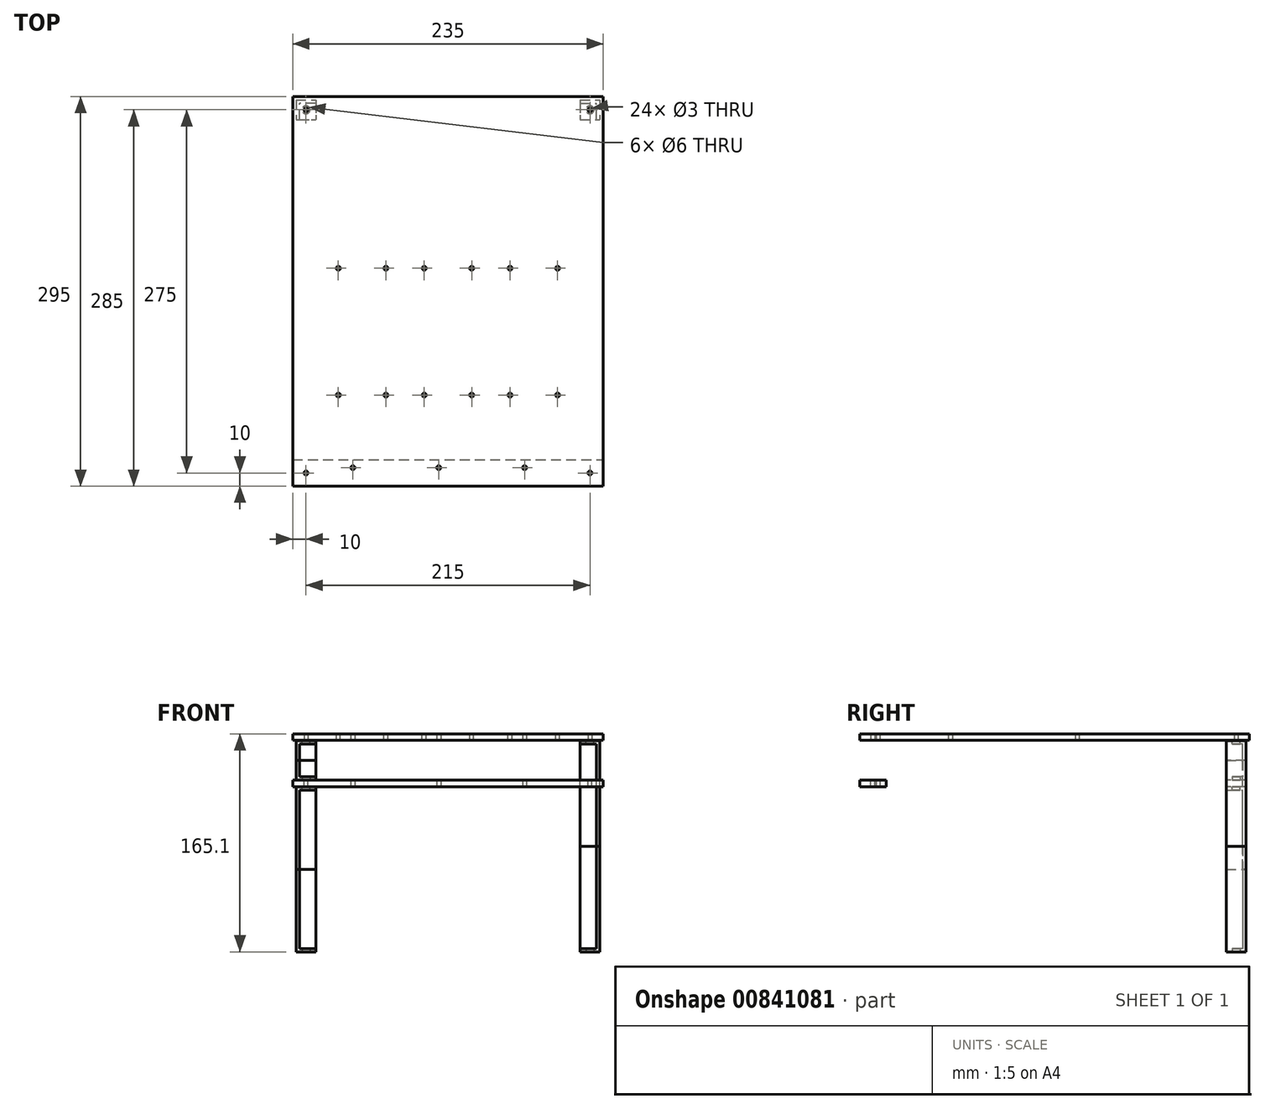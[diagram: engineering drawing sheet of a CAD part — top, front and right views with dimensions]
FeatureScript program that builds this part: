
annotation { "Feature Type Name" : "Feature", "Feature Type Description" : "" }
export const myFeature = defineFeature(function(context is Context, id is Id, definition is map)
    precondition{}
    {
        {
            var Q0;
            Q0=qCreatedBy(makeId("Top.planeOp"),FACE);
            var sketch = newSketch(context, id + "F0", { "sketchPlane" : qUnion([Q0])});
            skLineSegment(sketch, "E0.bottom", {"start": v(-22.5, 0) * mm, "end": v(22.5, 0) * mm});
            skLineSegment(sketch, "E0.top", {"start": v(-22.5, 130) * mm, "end": v(22.5, 130) * mm});
            skLineSegment(sketch, "E0.left", {"start": v(-22.5, 0) * mm, "end": v(-22.5, 130) * mm});
            skLineSegment(sketch, "E0.right", {"start": v(22.5, 0) * mm, "end": v(22.5, 130) * mm});
            skLineSegment(sketch, "E1.bottom", {"start": v(42.5, 0) * mm, "end": v(87.5, 0) * mm});
            skLineSegment(sketch, "E1.top", {"start": v(42.5, 130) * mm, "end": v(87.5, 130) * mm});
            skLineSegment(sketch, "E1.left", {"start": v(42.5, 0) * mm, "end": v(42.5, 130) * mm});
            skLineSegment(sketch, "E1.right", {"start": v(87.5, 0) * mm, "end": v(87.5, 130) * mm});
            skLineSegment(sketch, "E2.bottom", {"start": v(-42.5, 0) * mm, "end": v(-87.5, 0) * mm});
            skLineSegment(sketch, "E2.top", {"start": v(-42.5, 130) * mm, "end": v(-87.5, 130) * mm});
            skLineSegment(sketch, "E2.left", {"start": v(-42.5, 0) * mm, "end": v(-42.5, 130) * mm});
            skLineSegment(sketch, "E2.right", {"start": v(-87.5, 0) * mm, "end": v(-87.5, 130) * mm});
            skCircle(sketch, "E3", {"center": v(-83, 4) * mm, "radius": 1.5 * mm});
            skCircle(sketch, "E4", {"center": v(-47, 4) * mm, "radius": 1.5 * mm});
            skCircle(sketch, "E5", {"center": v(-47, 100) * mm, "radius": 1.5 * mm});
            skCircle(sketch, "E6", {"center": v(-83, 100) * mm, "radius": 1.5 * mm});
            skLineSegment(sketch, "E7", {"start": v(-47, 100) * mm, "end": v(-47, 4) * mm, "construction": true});
            skLineSegment(sketch, "E8", {"start": v(-47, 52) * mm, "end": v(0, 52) * mm, "construction": true});
            skLineSegment(sketch, "E9", {"start": v(0, 52) * mm, "end": v(65, 52) * mm, "construction": true});
            skPoint(sketch, "E9.endSnap0", {"position": v(65, 0) * mm});
            skLineSegment(sketch, "E10.bottom", {"start": v(-18, 4) * mm, "end": v(18, 4) * mm, "construction": true});
            skLineSegment(sketch, "E10.top", {"start": v(-18, 100) * mm, "end": v(18, 100) * mm, "construction": true});
            skLineSegment(sketch, "E10.left", {"start": v(-18, 4) * mm, "end": v(-18, 100) * mm, "construction": true});
            skLineSegment(sketch, "E10.right", {"start": v(18, 4) * mm, "end": v(18, 100) * mm, "construction": true});
            skPoint(sketch, "E10.middle", {"position": v(0, 52) * mm});
            skLineSegment(sketch, "E11.bottom", {"start": v(83, 4) * mm, "end": v(47, 4) * mm, "construction": true});
            skLineSegment(sketch, "E11.top", {"start": v(83, 100) * mm, "end": v(47, 100) * mm, "construction": true});
            skLineSegment(sketch, "E11.left", {"start": v(83, 4) * mm, "end": v(83, 100) * mm, "construction": true});
            skLineSegment(sketch, "E11.right", {"start": v(47, 4) * mm, "end": v(47, 100) * mm, "construction": true});
            skPoint(sketch, "E11.middle", {"position": v(65, 52) * mm});
            skCircle(sketch, "E12", {"center": v(-18, 100) * mm, "radius": 1.5 * mm});
            skCircle(sketch, "E13", {"center": v(18, 100) * mm, "radius": 1.5 * mm});
            skCircle(sketch, "E14", {"center": v(18, 4) * mm, "radius": 1.5 * mm});
            skCircle(sketch, "E15", {"center": v(-18, 4) * mm, "radius": 1.5 * mm});
            skCircle(sketch, "E16", {"center": v(47, 4) * mm, "radius": 1.5 * mm});
            skCircle(sketch, "E17", {"center": v(83, 4) * mm, "radius": 1.5 * mm});
            skCircle(sketch, "E18", {"center": v(47, 100) * mm, "radius": 1.5 * mm});
            skCircle(sketch, "E19", {"center": v(83, 100) * mm, "radius": 1.5 * mm});
            skLineSegment(sketch, "E20", {"start": v(-72, 42.63) * mm, "end": v(-72, -107.37) * mm, "construction": true});
            skLineSegment(sketch, "E21", {"start": v(-7, 42.63) * mm, "end": v(-7, -107.37) * mm, "construction": true});
            skLineSegment(sketch, "E22", {"start": v(58, 42.63) * mm, "end": v(58, -107.37) * mm, "construction": true});
            skSolve(sketch);
        }
        {
            var Q0;
            Q0=qCreatedBy(makeId("Top.planeOp"),FACE);
            var sketch = newSketch(context, id + "F1", { "sketchPlane" : qUnion([Q0])});
            skLineSegment(sketch, "E23.bottom", {"start": v(-117.5, 230) * mm, "end": v(117.5, 230) * mm});
            skLineSegment(sketch, "E23.top", {"start": v(-117.5, -65) * mm, "end": v(117.5, -65) * mm});
            skLineSegment(sketch, "E23.left", {"start": v(-117.5, 230) * mm, "end": v(-117.5, -65) * mm});
            skLineSegment(sketch, "E23.right", {"start": v(117.5, 230) * mm, "end": v(117.5, -65) * mm});
            skLineSegment(sketch, "E24", {"start": v(-117.5, -45) * mm, "end": v(117.5, -45) * mm, "construction": true});
            skSolve(sketch);
        }
        {
            var Q0;
            Q0=makeQuery(id+"F1.imprint","IMPRINT",FACE,{"disambiguationData":[TD([[makeQuery(id+"F1.imprint","IMPRINT",EDGE,{"derivedFrom":sQuery(id+"F1.wireOp",EDGE,"E23.bottom")}),-1.0]])]});
            extrude(context, id + "F2", {"entities" : qUnion([Q0]), "oppositeDirection" : true, "depth" : 5 * mm, "offsetDistance" : 25 * mm});
        }
        {
            var Q0;
            Q0=makeQuery(id+"F0.imprint","IMPRINT",FACE,{"disambiguationData":[TD([[makeQuery(id+"F0.imprint","IMPRINT",EDGE,{"derivedFrom":sQuery(id+"F0.wireOp",EDGE,"E5")}),1.0]])]});
            var Q1;
            Q1=makeQuery(id+"F0.imprint","IMPRINT",FACE,{"disambiguationData":[TD([[makeQuery(id+"F0.imprint","IMPRINT",EDGE,{"derivedFrom":sQuery(id+"F0.wireOp",EDGE,"E6")}),1.0]])]});
            var Q2;
            Q2=makeQuery(id+"F0.imprint","IMPRINT",FACE,{"disambiguationData":[TD([[makeQuery(id+"F0.imprint","IMPRINT",EDGE,{"derivedFrom":sQuery(id+"F0.wireOp",EDGE,"E3")}),1.0]])]});
            var Q3;
            Q3=makeQuery(id+"F0.imprint","IMPRINT",FACE,{"disambiguationData":[TD([[makeQuery(id+"F0.imprint","IMPRINT",EDGE,{"derivedFrom":sQuery(id+"F0.wireOp",EDGE,"E4")}),1.0]])]});
            var Q4;
            Q4=makeQuery(id+"F0.imprint","IMPRINT",FACE,{"disambiguationData":[TD([[makeQuery(id+"F0.imprint","IMPRINT",EDGE,{"derivedFrom":sQuery(id+"F0.wireOp",EDGE,"E15")}),1.0]])]});
            var Q5;
            Q5=makeQuery(id+"F0.imprint","IMPRINT",FACE,{"disambiguationData":[TD([[makeQuery(id+"F0.imprint","IMPRINT",EDGE,{"derivedFrom":sQuery(id+"F0.wireOp",EDGE,"E14")}),1.0]])]});
            var Q6;
            Q6=makeQuery(id+"F0.imprint","IMPRINT",FACE,{"disambiguationData":[TD([[makeQuery(id+"F0.imprint","IMPRINT",EDGE,{"derivedFrom":sQuery(id+"F0.wireOp",EDGE,"E12")}),1.0]])]});
            var Q7;
            Q7=makeQuery(id+"F0.imprint","IMPRINT",FACE,{"disambiguationData":[TD([[makeQuery(id+"F0.imprint","IMPRINT",EDGE,{"derivedFrom":sQuery(id+"F0.wireOp",EDGE,"E13")}),1.0]])]});
            var Q8;
            Q8=makeQuery(id+"F0.imprint","IMPRINT",FACE,{"disambiguationData":[TD([[makeQuery(id+"F0.imprint","IMPRINT",EDGE,{"derivedFrom":sQuery(id+"F0.wireOp",EDGE,"E18")}),1.0]])]});
            var Q9;
            Q9=makeQuery(id+"F0.imprint","IMPRINT",FACE,{"disambiguationData":[TD([[makeQuery(id+"F0.imprint","IMPRINT",EDGE,{"derivedFrom":sQuery(id+"F0.wireOp",EDGE,"E19")}),1.0]])]});
            var Q10;
            Q10=makeQuery(id+"F0.imprint","IMPRINT",FACE,{"disambiguationData":[TD([[makeQuery(id+"F0.imprint","IMPRINT",EDGE,{"derivedFrom":sQuery(id+"F0.wireOp",EDGE,"E17")}),1.0]])]});
            var Q11;
            Q11=makeQuery(id+"F0.imprint","IMPRINT",FACE,{"disambiguationData":[TD([[makeQuery(id+"F0.imprint","IMPRINT",EDGE,{"derivedFrom":sQuery(id+"F0.wireOp",EDGE,"E16")}),1.0]])]});
            extrude(context, id + "F3", {"entities" : qUnion([Q0, Q1, Q2, Q3, Q4, Q5, Q6, Q7, Q8, Q9, Q10, Q11]), "operationType" : NewBodyOperationType.REMOVE, "endBound" : BoundingType.THROUGH_ALL, "oppositeDirection" : true, "depth" : 25 * mm, "offsetDistance" : 25 * mm});
        }
        {
            var Q0;
            Q0=makeQuery(id+"F2.opExtrude","CAP_FACE",FACE,{"disambiguationData":[OSD([sQuery(id+"F1.wireOp",EDGE,"E23.bottom"),sQuery(id+"F1.wireOp",EDGE,"E23.top"),sQuery(id+"F1.wireOp",EDGE,"E23.left"),sQuery(id+"F1.wireOp",EDGE,"E23.right")])],"isStart":false});
            var sketch = newSketch(context, id + "F4", { "sketchPlane" : qUnion([Q0])});
            skLineSegment(sketch, "E25", {"start": v(117.5, -230) * mm, "end": v(-117.5, 65) * mm, "construction": true});
            skLineSegment(sketch, "E26.bottom", {"start": v(107.5, 55) * mm, "end": v(-107.5, 55) * mm, "construction": true});
            skLineSegment(sketch, "E26.top", {"start": v(107.5, -220) * mm, "end": v(-107.5, -220) * mm, "construction": true});
            skLineSegment(sketch, "E26.left", {"start": v(107.5, 55) * mm, "end": v(107.5, -220) * mm, "construction": true});
            skLineSegment(sketch, "E26.right", {"start": v(-107.5, 55) * mm, "end": v(-107.5, -220) * mm, "construction": true});
            skPoint(sketch, "E26.middle", {"position": v(0, -82.5) * mm});
            skCircle(sketch, "E27", {"center": v(107.5, -220) * mm, "radius": 1.5 * mm});
            skCircle(sketch, "E28", {"center": v(-107.5, -220) * mm, "radius": 1.5 * mm});
            skCircle(sketch, "E29", {"center": v(-107.5, 55) * mm, "radius": 1.5 * mm});
            skCircle(sketch, "E30", {"center": v(107.5, 55) * mm, "radius": 1.5 * mm});
            skSolve(sketch);
        }
        {
            var Q0;
            Q0=makeQuery(id+"F4.imprint","IMPRINT",FACE,{"disambiguationData":[TD([[makeQuery(id+"F4.imprint","IMPRINT",EDGE,{"derivedFrom":sQuery(id+"F4.wireOp",EDGE,"E27")}),1.0]])]});
            var Q1;
            Q1=makeQuery(id+"F4.imprint","IMPRINT",FACE,{"disambiguationData":[TD([[makeQuery(id+"F4.imprint","IMPRINT",EDGE,{"derivedFrom":sQuery(id+"F4.wireOp",EDGE,"E30")}),1.0]])]});
            var Q2;
            Q2=makeQuery(id+"F4.imprint","IMPRINT",FACE,{"disambiguationData":[TD([[makeQuery(id+"F4.imprint","IMPRINT",EDGE,{"derivedFrom":sQuery(id+"F4.wireOp",EDGE,"E29")}),1.0]])]});
            var Q3;
            Q3=makeQuery(id+"F4.imprint","IMPRINT",FACE,{"disambiguationData":[TD([[makeQuery(id+"F4.imprint","IMPRINT",EDGE,{"derivedFrom":sQuery(id+"F4.wireOp",EDGE,"E28")}),1.0]])]});
            var Q4;
            Q4=sQuery(id+"F4.wireOp",EDGE,"E27");
            extrude(context, id + "F5", {"entities" : qUnion([Q0, Q1, Q2, Q3]), "operationType" : NewBodyOperationType.REMOVE, "surfaceEntities" : qUnion([Q4]), "endBound" : BoundingType.THROUGH_ALL, "oppositeDirection" : true, "depth" : 25 * mm, "offsetDistance" : 25 * mm});
        }
        {
            var Q0;
            Q0=makeQuery(id+"F2.opExtrude","CAP_FACE",FACE,{"disambiguationData":[OSD([sQuery(id+"F1.wireOp",EDGE,"E23.bottom"),sQuery(id+"F1.wireOp",EDGE,"E23.top"),sQuery(id+"F1.wireOp",EDGE,"E23.left"),sQuery(id+"F1.wireOp",EDGE,"E23.right")])],"isStart":false});
            cPlane(context, id + "F6", {"entities" : qUnion([Q0]), "cplaneType" : CPlaneType.OFFSET, "offset" : 0.1 * mm, "width" : 150 * mm, "height" : 150 * mm});
        }
        {
            var Q0;
            Q0=qCreatedBy(id+"F6.planeOp",FACE);
            var sketch = newSketch(context, id + "F7", { "sketchPlane" : qUnion([Q0])});
            skCircle(sketch, "E31.0", {"center": v(-107.5, -220) * mm, "radius": 1.5 * mm, "construction": true});
            skCircle(sketch, "E32", {"center": v(-107.5, -220) * mm, "radius": 3 * mm});
            skLineSegment(sketch, "E33.bottom", {"start": v(-115, -227.5) * mm, "end": v(-100, -227.5) * mm});
            skLineSegment(sketch, "E33.top", {"start": v(-115, -212.5) * mm, "end": v(-100, -212.5) * mm});
            skLineSegment(sketch, "E33.left", {"start": v(-115, -227.5) * mm, "end": v(-115, -212.5) * mm});
            skLineSegment(sketch, "E33.right", {"start": v(-100, -227.5) * mm, "end": v(-100, -212.5) * mm});
            skSolve(sketch);
        }
        {
            var Q0;
            Q0=makeQuery(id+"F7.imprint","IMPRINT",FACE,{"disambiguationData":[TD([[makeQuery(id+"F7.imprint","IMPRINT",EDGE,{"derivedFrom":sQuery(id+"F7.wireOp",EDGE,"E32")}),-1.0]])]});
            extrude(context, id + "F8", {"entities" : qUnion([Q0]), "depth" : 2.5 * mm, "offsetDistance" : 25 * mm});
        }
        {
            var Q0;
            Q0=makeQuery(id+"F8.opExtrude","CAP_FACE",FACE,{"disambiguationData":[OSD([sQuery(id+"F7.wireOp",EDGE,"E32"),sQuery(id+"F7.wireOp",EDGE,"E33.bottom"),sQuery(id+"F7.wireOp",EDGE,"E33.top"),sQuery(id+"F7.wireOp",EDGE,"E33.left"),sQuery(id+"F7.wireOp",EDGE,"E33.right")])],"isStart":false});
            var sketch = newSketch(context, id + "F9", { "sketchPlane" : qUnion([Q0])});
            skLineSegment(sketch, "E34", {"start": v(-115, -212.5) * mm, "end": v(-112.5, -212.5) * mm});
            skLineSegment(sketch, "E35", {"start": v(-112.5, -212.5) * mm, "end": v(-112.5, -227.5) * mm});
            skLineSegment(sketch, "E36", {"start": v(-112.5, -227.5) * mm, "end": v(-115, -227.5) * mm});
            skLineSegment(sketch, "E37", {"start": v(-115, -227.5) * mm, "end": v(-115, -212.5) * mm});
            skLineSegment(sketch, "E38", {"start": v(-100, -227.5) * mm, "end": v(-100, -225) * mm});
            skLineSegment(sketch, "E39", {"start": v(-100, -225) * mm, "end": v(-115, -225) * mm});
            skLineSegment(sketch, "E40", {"start": v(-115, -225) * mm, "end": v(-115, -227.5) * mm});
            skSolve(sketch);
        }
        {
            var Q0;
            {var subQ0=sQuery(id+"F9.wireOp",EDGE,"E34");Q0=makeQuery(id+"F9.imprint","IMPRINT",FACE,{"disambiguationData":[TD([[makeQuery(id+"F9.imprint","IMPRINT",EDGE,{"derivedFrom":subQ0}),-1.0]])]});}
            var Q1;
            {var subQ0=sQuery(id+"F9.wireOp",EDGE,"E36");Q1=makeQuery(id+"F9.imprint","IMPRINT",FACE,{"disambiguationData":[TD([[makeQuery(id+"F9.imprint","IMPRINT",EDGE,{"derivedFrom":subQ0}),1.0]])]});}
            var Q2;
            {var subQ5=sQuery(id+"F9.wireOp",EDGE,"E38");Q2=makeQuery(id+"F9.imprint","IMPRINT",FACE,{"disambiguationData":[TD([[makeQuery(id+"F9.imprint","IMPRINT",EDGE,{"derivedFrom":subQ5}),1.0]])]});}
            extrude(context, id + "F10", {"entities" : qUnion([Q0, Q1, Q2]), "operationType" : NewBodyOperationType.ADD, "depth" : 12.5 * mm, "offsetDistance" : 25 * mm});
        }
        {
            var Q0;
            Q0=makeQuery(id+"F8.opExtrude","SWEPT_BODY",BODY,{"disambiguationData":[OSD([sQuery(id+"F7.wireOp",EDGE,"E32"),sQuery(id+"F7.wireOp",EDGE,"E33.bottom"),sQuery(id+"F7.wireOp",EDGE,"E33.top"),sQuery(id+"F7.wireOp",EDGE,"E33.left"),sQuery(id+"F7.wireOp",EDGE,"E33.right")])]});
            var Q1;
            Q1=makeQuery(id+"F10.opExtrude","CAP_FACE",FACE,{"disambiguationData":[OSD([sQuery(id+"F7.wireOp",EDGE,"E33.bottom"),sQuery(id+"F9.wireOp",EDGE,"E34"),sQuery(id+"F9.wireOp",EDGE,"E35"),sQuery(id+"F9.wireOp",EDGE,"E36"),sQuery(id+"F9.wireOp",EDGE,"E37"),sQuery(id+"F9.wireOp",EDGE,"E38"),sQuery(id+"F9.wireOp",EDGE,"E39"),sQuery(id+"F9.wireOp",EDGE,"E40")])],"isStart":false});
            mirror(context, id + "F11", {"operationType" : NewBodyOperationType.ADD, "entities" : qUnion([Q0]), "mirrorPlane" : qUnion([Q1])});
        }
        {
            var Q0;
            Q0=makeQuery(id+"F2.opExtrude","CAP_FACE",FACE,{"disambiguationData":[OSD([sQuery(id+"F1.wireOp",EDGE,"E23.bottom"),sQuery(id+"F1.wireOp",EDGE,"E23.top"),sQuery(id+"F1.wireOp",EDGE,"E23.left"),sQuery(id+"F1.wireOp",EDGE,"E23.right")])],"isStart":false});
            cPlane(context, id + "F12", {"entities" : qUnion([Q0]), "cplaneType" : CPlaneType.OFFSET, "offset" : 30 * mm, "width" : 150 * mm, "height" : 150 * mm});
        }
        {
            var Q0;
            Q0=qCreatedBy(id+"F12.planeOp",FACE);
            var sketch = newSketch(context, id + "F13", { "sketchPlane" : qUnion([Q0])});
            skLineSegment(sketch, "E41.0", {"start": v(-117.5, 65) * mm, "end": v(117.5, 65) * mm});
            skCircle(sketch, "E42.0", {"center": v(-107.5, 55) * mm, "radius": 1.5 * mm});
            skCircle(sketch, "E43.0", {"center": v(107.5, 55) * mm, "radius": 1.5 * mm});
            skLineSegment(sketch, "E44", {"start": v(-117.5, 65) * mm, "end": v(-117.5, 45) * mm});
            skLineSegment(sketch, "E45", {"start": v(-117.5, 45) * mm, "end": v(117.5, 45) * mm});
            skLineSegment(sketch, "E46", {"start": v(117.5, 45) * mm, "end": v(117.5, 65) * mm});
            skSolve(sketch);
        }
        {
            var Q0;
            Q0=makeQuery(id+"F13.imprint","IMPRINT",FACE,{"disambiguationData":[TD([[makeQuery(id+"F13.imprint","IMPRINT",EDGE,{"derivedFrom":sQuery(id+"F13.wireOp",EDGE,"E41.0")}),-1.0]])]});
            extrude(context, id + "F14", {"entities" : qUnion([Q0]), "depth" : 5 * mm, "offsetDistance" : 25 * mm});
        }
        {
            var Q0;
            Q0=makeQuery(id+"F14.opExtrude","CAP_FACE",FACE,{"disambiguationData":[OSD([sQuery(id+"F13.wireOp",EDGE,"E41.0"),sQuery(id+"F13.wireOp",EDGE,"E42.0"),sQuery(id+"F13.wireOp",EDGE,"E43.0"),sQuery(id+"F13.wireOp",EDGE,"E44"),sQuery(id+"F13.wireOp",EDGE,"E45"),sQuery(id+"F13.wireOp",EDGE,"E46")])],"isStart":false});
            var sketch = newSketch(context, id + "F15", { "sketchPlane" : qUnion([Q0])});
            skLineSegment(sketch, "E47.0", {"start": v(-72, -42.63) * mm, "end": v(-72, 107.37) * mm, "construction": true});
            skLineSegment(sketch, "E48.0", {"start": v(-7, -42.63) * mm, "end": v(-7, 107.37) * mm, "construction": true});
            skLineSegment(sketch, "E49.0", {"start": v(58, -42.63) * mm, "end": v(58, 107.37) * mm, "construction": true});
            skPoint(sketch, "E50", {"position": v(-72, 51) * mm});
            skPoint(sketch, "E51", {"position": v(-7, 51) * mm});
            skPoint(sketch, "E52", {"position": v(58, 51) * mm});
            skCircle(sketch, "E53", {"center": v(-72, 51) * mm, "radius": 1.5 * mm});
            skCircle(sketch, "E54", {"center": v(-7, 51) * mm, "radius": 1.5 * mm});
            skCircle(sketch, "E55", {"center": v(58, 51) * mm, "radius": 1.5 * mm});
            skSolve(sketch);
        }
        {
            var Q0;
            Q0 = qSketchRegion(id + "F15", true);
            extrude(context, id + "F16", {"entities" : qUnion([Q0]), "operationType" : NewBodyOperationType.REMOVE, "endBound" : BoundingType.THROUGH_ALL, "oppositeDirection" : true, "depth" : 25 * mm, "offsetDistance" : 25 * mm});
        }
        {
            var Q0;
            Q0=qCreatedBy(id+"F6.planeOp",FACE);
            var sketch = newSketch(context, id + "F17", { "sketchPlane" : qUnion([Q0])});
            skCircle(sketch, "E56.0", {"center": v(107.5, -220) * mm, "radius": 1.5 * mm});
            skCircle(sketch, "E57", {"center": v(107.5, -220) * mm, "radius": 3 * mm});
            skLineSegment(sketch, "E58.bottom", {"start": v(100, -227.5) * mm, "end": v(115, -227.5) * mm});
            skLineSegment(sketch, "E58.top", {"start": v(100, -212.5) * mm, "end": v(115, -212.5) * mm});
            skLineSegment(sketch, "E58.left", {"start": v(100, -227.5) * mm, "end": v(100, -212.5) * mm});
            skLineSegment(sketch, "E58.right", {"start": v(115, -227.5) * mm, "end": v(115, -212.5) * mm});
            skSolve(sketch);
        }
        {
            var Q0;
            Q0=makeQuery(id+"F17.imprint","IMPRINT",FACE,{"disambiguationData":[TD([[makeQuery(id+"F17.imprint","IMPRINT",EDGE,{"derivedFrom":sQuery(id+"F17.wireOp",EDGE,"E57")}),-1.0]])]});
            extrude(context, id + "F18", {"entities" : qUnion([Q0]), "depth" : 2.5 * mm, "offsetDistance" : 25 * mm});
        }
        {
            var Q0;
            Q0=makeQuery(id+"F18.opExtrude","CAP_FACE",FACE,{"disambiguationData":[OSD([sQuery(id+"F17.wireOp",EDGE,"E57"),sQuery(id+"F17.wireOp",EDGE,"E58.bottom"),sQuery(id+"F17.wireOp",EDGE,"E58.top"),sQuery(id+"F17.wireOp",EDGE,"E58.left"),sQuery(id+"F17.wireOp",EDGE,"E58.right")])],"isStart":false});
            var sketch = newSketch(context, id + "F19", { "sketchPlane" : qUnion([Q0])});
            skLineSegment(sketch, "E59", {"start": v(100, -227.5) * mm, "end": v(100, -225) * mm});
            skLineSegment(sketch, "E60", {"start": v(100, -225) * mm, "end": v(115, -225) * mm});
            skLineSegment(sketch, "E61", {"start": v(115, -225) * mm, "end": v(115, -227.5) * mm});
            skLineSegment(sketch, "E62", {"start": v(115, -227.5) * mm, "end": v(100, -227.5) * mm});
            skLineSegment(sketch, "E63", {"start": v(115, -212.5) * mm, "end": v(112.5, -212.5) * mm});
            skLineSegment(sketch, "E64", {"start": v(112.5, -212.5) * mm, "end": v(112.5, -227.5) * mm});
            skLineSegment(sketch, "E65", {"start": v(112.5, -227.5) * mm, "end": v(115, -227.5) * mm});
            skSolve(sketch);
        }
        {
            var Q0;
            {var subQ0=sQuery(id+"F19.wireOp",EDGE,"E59");Q0=makeQuery(id+"F19.imprint","IMPRINT",FACE,{"disambiguationData":[TD([[makeQuery(id+"F19.imprint","IMPRINT",EDGE,{"derivedFrom":subQ0}),-1.0]])]});}
            var Q1;
            {var subQ0=sQuery(id+"F19.wireOp",EDGE,"E61");Q1=makeQuery(id+"F19.imprint","IMPRINT",FACE,{"disambiguationData":[TD([[makeQuery(id+"F19.imprint","IMPRINT",EDGE,{"derivedFrom":subQ0}),1.0]])]});}
            var Q2;
            {var subQ5=sQuery(id+"F19.wireOp",EDGE,"E63");Q2=makeQuery(id+"F19.imprint","IMPRINT",FACE,{"disambiguationData":[TD([[makeQuery(id+"F19.imprint","IMPRINT",EDGE,{"derivedFrom":subQ5}),-1.0]])]});}
            extrude(context, id + "F20", {"entities" : qUnion([Q0, Q1, Q2]), "operationType" : NewBodyOperationType.ADD, "depth" : 77.5 * mm, "offsetDistance" : 25 * mm});
        }
        {
            var Q0;
            Q0=makeQuery(id+"F18.opExtrude","SWEPT_BODY",BODY,{"disambiguationData":[OSD([sQuery(id+"F17.wireOp",EDGE,"E57"),sQuery(id+"F17.wireOp",EDGE,"E58.bottom"),sQuery(id+"F17.wireOp",EDGE,"E58.top"),sQuery(id+"F17.wireOp",EDGE,"E58.left"),sQuery(id+"F17.wireOp",EDGE,"E58.right")])]});
            var Q1;
            Q1=makeQuery(id+"F20.opExtrude","CAP_FACE",FACE,{"disambiguationData":[OSD([sQuery(id+"F17.wireOp",EDGE,"E58.right"),sQuery(id+"F19.wireOp",EDGE,"E59"),sQuery(id+"F19.wireOp",EDGE,"E60"),sQuery(id+"F19.wireOp",EDGE,"E61"),sQuery(id+"F19.wireOp",EDGE,"E62"),sQuery(id+"F19.wireOp",EDGE,"E63"),sQuery(id+"F19.wireOp",EDGE,"E64"),sQuery(id+"F19.wireOp",EDGE,"E65")])],"isStart":false});
            mirror(context, id + "F21", {"operationType" : NewBodyOperationType.ADD, "entities" : qUnion([Q0]), "mirrorPlane" : qUnion([Q1])});
        }
        {
            var Q0;
            Q0=makeQuery(id+"F11.opPattern","COPY",FACE,{"derivedFrom":makeQuery(id+"F8.opExtrude","CAP_FACE",FACE,{"disambiguationData":[OSD([sQuery(id+"F7.wireOp",EDGE,"E32"),sQuery(id+"F7.wireOp",EDGE,"E33.bottom"),sQuery(id+"F7.wireOp",EDGE,"E33.top"),sQuery(id+"F7.wireOp",EDGE,"E33.left"),sQuery(id+"F7.wireOp",EDGE,"E33.right")])],"isStart":true}),"instanceName":"1"});
            cPlane(context, id + "F22", {"entities" : qUnion([Q0]), "cplaneType" : CPlaneType.OFFSET, "offset" : 5 * mm, "width" : 150 * mm, "height" : 150 * mm});
        }
        {
            var Q0;
            Q0=qCreatedBy(id+"F22.planeOp",FACE);
            var sketch = newSketch(context, id + "F23", { "sketchPlane" : qUnion([Q0])});
            skCircle(sketch, "E66.0", {"center": v(-107.5, -220) * mm, "radius": 3 * mm});
            skLineSegment(sketch, "E67.0.0", {"start": v(-100, -212.5) * mm, "end": v(-115, -212.5) * mm});
            skLineSegment(sketch, "E67.0.1", {"start": v(-115, -212.5) * mm, "end": v(-115, -227.5) * mm});
            skLineSegment(sketch, "E67.0.2", {"start": v(-115, -227.5) * mm, "end": v(-100, -227.5) * mm});
            skLineSegment(sketch, "E67.0.3", {"start": v(-100, -227.5) * mm, "end": v(-100, -212.5) * mm});
            skSolve(sketch);
        }
        {
            var Q0;
            Q0=makeQuery(id+"F23.imprint","IMPRINT",FACE,{"disambiguationData":[TD([[makeQuery(id+"F23.imprint","IMPRINT",EDGE,{"derivedFrom":sQuery(id+"F23.wireOp",EDGE,"E66.0")}),-1.0]])]});
            extrude(context, id + "F24", {"entities" : qUnion([Q0]), "depth" : 2.5 * mm, "offsetDistance" : 25 * mm});
        }
        {
            var Q0;
            Q0=makeQuery(id+"F24.opExtrude","CAP_FACE",FACE,{"disambiguationData":[OSD([sQuery(id+"F23.wireOp",EDGE,"E66.0"),sQuery(id+"F23.wireOp",EDGE,"E67.0.0"),sQuery(id+"F23.wireOp",EDGE,"E67.0.1"),sQuery(id+"F23.wireOp",EDGE,"E67.0.2"),sQuery(id+"F23.wireOp",EDGE,"E67.0.3")])],"isStart":false});
            var sketch = newSketch(context, id + "F25", { "sketchPlane" : qUnion([Q0])});
            skLineSegment(sketch, "E68", {"start": v(-100, -227.5) * mm, "end": v(-100, -225) * mm});
            skLineSegment(sketch, "E69", {"start": v(-100, -225) * mm, "end": v(-115, -225) * mm});
            skLineSegment(sketch, "E70", {"start": v(-115, -225) * mm, "end": v(-115, -227.5) * mm});
            skLineSegment(sketch, "E71", {"start": v(-115, -227.5) * mm, "end": v(-100, -227.5) * mm});
            skLineSegment(sketch, "E72", {"start": v(-115, -212.5) * mm, "end": v(-112.5, -212.5) * mm});
            skLineSegment(sketch, "E73", {"start": v(-112.5, -212.5) * mm, "end": v(-112.5, -227.5) * mm});
            skLineSegment(sketch, "E74", {"start": v(-112.5, -227.5) * mm, "end": v(-115, -227.5) * mm});
            skSolve(sketch);
        }
        {
            var Q0;
            Q0 = qSketchRegion(id + "F25", true);
            var Q1;
            {var subQ5=sQuery(id+"F25.wireOp",EDGE,"E72");Q1=makeQuery(id+"F25.imprint","IMPRINT",FACE,{"disambiguationData":[TD([[makeQuery(id+"F25.imprint","IMPRINT",EDGE,{"derivedFrom":subQ5}),1.0]])]});}
            extrude(context, id + "F26", {"entities" : qUnion([Q0, Q1]), "operationType" : NewBodyOperationType.ADD, "depth" : 60 * mm, "offsetDistance" : 25 * mm});
        }
        {
            var Q0;
            Q0=makeQuery(id+"F24.opExtrude","SWEPT_BODY",BODY,{"disambiguationData":[OSD([sQuery(id+"F23.wireOp",EDGE,"E66.0"),sQuery(id+"F23.wireOp",EDGE,"E67.0.0"),sQuery(id+"F23.wireOp",EDGE,"E67.0.1"),sQuery(id+"F23.wireOp",EDGE,"E67.0.2"),sQuery(id+"F23.wireOp",EDGE,"E67.0.3")])]});
            var Q1;
            Q1=makeQuery(id+"F26.opExtrude","CAP_FACE",FACE,{"disambiguationData":[OSD([sQuery(id+"F23.wireOp",EDGE,"E67.0.1"),sQuery(id+"F25.wireOp",EDGE,"E68"),sQuery(id+"F25.wireOp",EDGE,"E69"),sQuery(id+"F25.wireOp",EDGE,"E70"),sQuery(id+"F25.wireOp",EDGE,"E71"),sQuery(id+"F25.wireOp",EDGE,"E72"),sQuery(id+"F25.wireOp",EDGE,"E73"),sQuery(id+"F25.wireOp",EDGE,"E74")])],"isStart":false});
            mirror(context, id + "F27", {"operationType" : NewBodyOperationType.ADD, "entities" : qUnion([Q0]), "mirrorPlane" : qUnion([Q1])});
        }
    });
